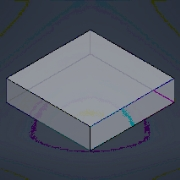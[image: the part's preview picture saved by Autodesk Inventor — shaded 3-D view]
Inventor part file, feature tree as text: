
AUTODESK INVENTOR PART (.ipt)
format: ipt  version: 2024.3 (Build 283343000, 343)  size: 134,656 bytes
history: native  units: mm
features: extrude x1, sketch x1
ambient origin geometry x8: Origin, YZ Plane, XZ Plane, XY Plane, X Axis, Y Axis, Z Axis, Center Point
bodies: Solid1 (feature_tree)
feature tree (2):
  extrude  "Extrusion1"  Depth=55.0mm
  sketch  "Sketch1"  dims[d0=100.0mm d1=55.0mm d2=25.0mm d3=0.0mm]
